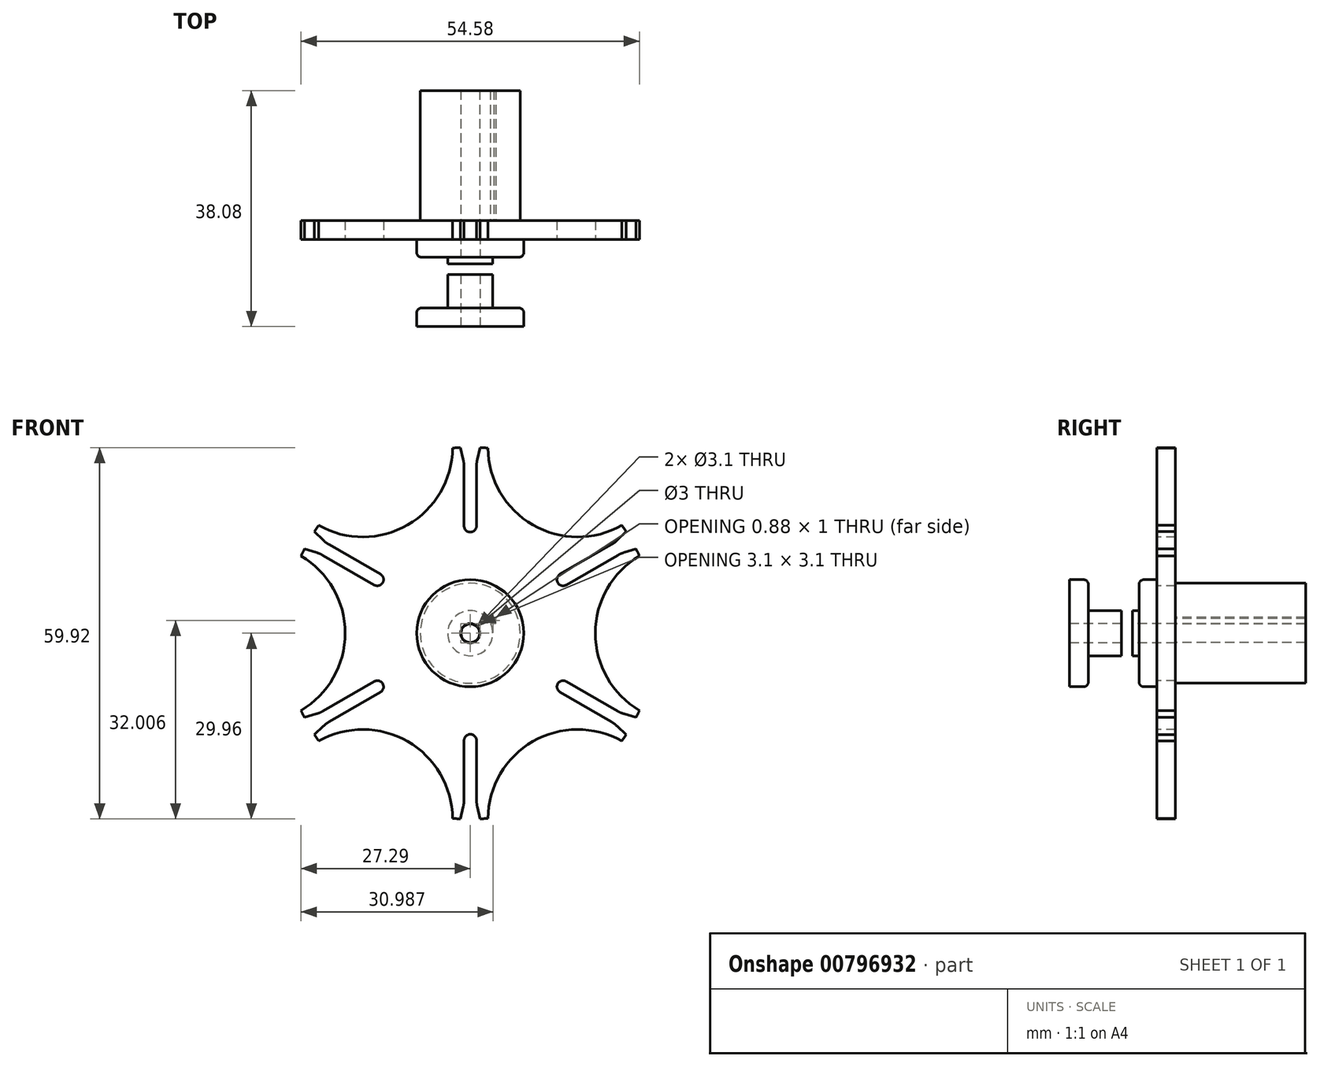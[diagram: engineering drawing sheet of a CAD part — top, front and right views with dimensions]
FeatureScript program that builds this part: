
annotation { "Feature Type Name" : "Feature", "Feature Type Description" : "" }
export const myFeature = defineFeature(function(context is Context, id is Id, definition is map)
    precondition{}
    {
        {
            var Q0;
            Q0=qCreatedBy(makeId("Front.planeOp"),FACE);
            var sketch = newSketch(context, id + "F0", { "sketchPlane" : qUnion([Q0])});
            skCircle(sketch, "E0", {"center": v(0, 0) * mm, "radius": 8.06 * mm});
            skCircle(sketch, "E1", {"center": v(0, 0) * mm, "radius": 3.64 * mm});
            skLineSegment(sketch, "E2", {"start": v(0.57, 3.6) * mm, "end": v(0.57, 4.1) * mm});
            skLineSegment(sketch, "E3", {"start": v(0.57, 4.1) * mm, "end": v(-0.57, 4.1) * mm});
            skLineSegment(sketch, "E4", {"start": v(-0.57, 4.1) * mm, "end": v(-0.57, 3.6) * mm});
            skLineSegment(sketch, "E5", {"start": v(-0.58, 4.1) * mm, "end": v(0, 4.78) * mm});
            skLineSegment(sketch, "E6", {"start": v(0, 4.78) * mm, "end": v(0.57, 4.1) * mm});
            skLineSegment(sketch, "E7.1.0", {"start": v(-3.83, 1.55) * mm, "end": v(-3.4, 1.3) * mm});
            skLineSegment(sketch, "E7.1.1", {"start": v(-2.82, 2.3) * mm, "end": v(-3.26, 2.54) * mm});
            skLineSegment(sketch, "E7.1.2", {"start": v(-3.83, 1.55) * mm, "end": v(-4.14, 2.39) * mm});
            skLineSegment(sketch, "E7.1.3", {"start": v(-4.14, 2.39) * mm, "end": v(-3.26, 2.54) * mm});
            skLineSegment(sketch, "E7.1.4", {"start": v(-3.26, 2.54) * mm, "end": v(-3.83, 1.55) * mm});
            skLineSegment(sketch, "E7.2.0", {"start": v(-3.26, -2.54) * mm, "end": v(-2.82, -2.3) * mm});
            skLineSegment(sketch, "E7.2.1", {"start": v(-3.4, -1.3) * mm, "end": v(-3.83, -1.55) * mm});
            skLineSegment(sketch, "E7.2.2", {"start": v(-3.26, -2.54) * mm, "end": v(-4.14, -2.39) * mm});
            skLineSegment(sketch, "E7.2.3", {"start": v(-4.14, -2.39) * mm, "end": v(-3.83, -1.55) * mm});
            skLineSegment(sketch, "E7.2.4", {"start": v(-3.83, -1.55) * mm, "end": v(-3.26, -2.54) * mm});
            skLineSegment(sketch, "E7.3.0", {"start": v(0.57, -4.1) * mm, "end": v(0.57, -3.6) * mm});
            skLineSegment(sketch, "E7.3.1", {"start": v(-0.58, -3.6) * mm, "end": v(-0.58, -4.1) * mm});
            skLineSegment(sketch, "E7.3.2", {"start": v(0.58, -4.1) * mm, "end": v(0, -4.78) * mm});
            skLineSegment(sketch, "E7.3.3", {"start": v(0, -4.78) * mm, "end": v(-0.58, -4.1) * mm});
            skLineSegment(sketch, "E7.3.4", {"start": v(-0.58, -4.1) * mm, "end": v(0.57, -4.1) * mm});
            skLineSegment(sketch, "E7.4.0", {"start": v(3.83, -1.55) * mm, "end": v(3.4, -1.3) * mm});
            skLineSegment(sketch, "E7.4.1", {"start": v(2.82, -2.3) * mm, "end": v(3.26, -2.54) * mm});
            skLineSegment(sketch, "E7.4.2", {"start": v(3.83, -1.55) * mm, "end": v(4.14, -2.39) * mm});
            skLineSegment(sketch, "E7.4.3", {"start": v(4.14, -2.39) * mm, "end": v(3.26, -2.54) * mm});
            skLineSegment(sketch, "E7.4.4", {"start": v(3.26, -2.54) * mm, "end": v(3.83, -1.55) * mm});
            skLineSegment(sketch, "E7.5.0", {"start": v(3.26, 2.54) * mm, "end": v(2.82, 2.3) * mm});
            skLineSegment(sketch, "E7.5.1", {"start": v(3.4, 1.3) * mm, "end": v(3.83, 1.55) * mm});
            skLineSegment(sketch, "E7.5.2", {"start": v(3.26, 2.54) * mm, "end": v(4.14, 2.39) * mm});
            skLineSegment(sketch, "E7.5.3", {"start": v(4.14, 2.39) * mm, "end": v(3.83, 1.55) * mm});
            skLineSegment(sketch, "E7.5.4", {"start": v(3.83, 1.55) * mm, "end": v(3.26, 2.54) * mm});
            skSolve(sketch);
        }
        {
            var Q0;
            Q0=qCreatedBy(makeId("Front.planeOp"),FACE);
            var sketch = newSketch(context, id + "F1", { "sketchPlane" : qUnion([Q0])});
            skCircle(sketch, "E8", {"center": v(0, 0) * mm, "radius": 30 * mm});
            skLineSegment(sketch, "E9", {"start": v(-1, 29.98) * mm, "end": v(1, 29.98) * mm});
            skLineSegment(sketch, "E10", {"start": v(1, 26.83) * mm, "end": v(1, 17.3) * mm});
            skArc(sketch, "E11", {"start": v(-1, 17.3) * mm, "mid": v(0, 16.3) * mm, "end": v(1, 17.3) * mm});
            skLineSegment(sketch, "E12", {"start": v(-1, 17.3) * mm, "end": v(-1, 26.83) * mm});
            skLineSegment(sketch, "E13", {"start": v(0, 0) * mm, "end": v(0, 9.56) * mm, "construction": true});
            skLineSegment(sketch, "E14", {"start": v(0, 0) * mm, "end": v(17.32, 30) * mm, "construction": true});
            skArc(sketch, "E15", {"start": v(24.44, 17.4) * mm, "mid": v(10.09, 17.47) * mm, "end": v(2.85, 29.86) * mm});
            skLineSegment(sketch, "E16", {"start": v(1.14, 28) * mm, "end": v(1.61, 29.96) * mm});
            skLineSegment(sketch, "E17", {"start": v(-1.14, 28) * mm, "end": v(-1.61, 29.96) * mm});
            skPoint(sketch, "E18.newPointA", {"position": v(-1, 27.43) * mm});
            skArc(sketch, "E18.filletArc", {"start": v(-1, 26.83) * mm, "mid": v(-1.04, 27.43) * mm, "end": v(-1.14, 28) * mm});
            skPoint(sketch, "E19.newPointA", {"position": v(1, 27.43) * mm});
            skPoint(sketch, "E19.newPointB", {"position": v(1, 29.98) * mm});
            skArc(sketch, "E19.filletArc", {"start": v(1.14, 28) * mm, "mid": v(1.04, 27.43) * mm, "end": v(1, 26.83) * mm});
            skArc(sketch, "E20.1.0", {"start": v(-15.49, 7.79) * mm, "mid": v(-14.12, 8.15) * mm, "end": v(-14.49, 9.52) * mm});
            skPoint(sketch, "E20.1.1", {"position": v(-25.47, 15.86) * mm});
            skPoint(sketch, "E20.1.2", {"position": v(-24.26, 12.85) * mm});
            skLineSegment(sketch, "E20.1.3", {"start": v(-22.74, 14.28) * mm, "end": v(-14.49, 9.52) * mm});
            skPoint(sketch, "E20.1.4", {"position": v(-23.26, 14.58) * mm});
            skLineSegment(sketch, "E20.1.5", {"start": v(-15.49, 7.79) * mm, "end": v(-23.74, 12.55) * mm});
            skArc(sketch, "E20.1.6", {"start": v(-2.85, 29.86) * mm, "mid": v(-10.09, 17.47) * mm, "end": v(-24.44, 17.4) * mm});
            skLineSegment(sketch, "E20.1.7", {"start": v(-26.47, 14.13) * mm, "end": v(-25.47, 15.86) * mm});
            skLineSegment(sketch, "E20.1.8", {"start": v(-24.83, 13.02) * mm, "end": v(-26.75, 13.58) * mm});
            skArc(sketch, "E20.1.9", {"start": v(-23.69, 15) * mm, "mid": v(-23.23, 14.6) * mm, "end": v(-22.74, 14.28) * mm});
            skLineSegment(sketch, "E20.1.10", {"start": v(-23.69, 15) * mm, "end": v(-25.14, 16.37) * mm});
            skArc(sketch, "E20.1.11", {"start": v(-23.74, 12.55) * mm, "mid": v(-24.27, 12.82) * mm, "end": v(-24.83, 13.02) * mm});
            skArc(sketch, "E20.2.0", {"start": v(-14.49, -9.52) * mm, "mid": v(-14.12, -8.15) * mm, "end": v(-15.49, -7.79) * mm});
            skPoint(sketch, "E20.2.1", {"position": v(-26.47, -14.13) * mm});
            skPoint(sketch, "E20.2.2", {"position": v(-23.26, -14.58) * mm});
            skLineSegment(sketch, "E20.2.3", {"start": v(-23.74, -12.55) * mm, "end": v(-15.49, -7.79) * mm});
            skPoint(sketch, "E20.2.4", {"position": v(-24.26, -12.85) * mm});
            skLineSegment(sketch, "E20.2.5", {"start": v(-14.49, -9.52) * mm, "end": v(-22.74, -14.28) * mm});
            skArc(sketch, "E20.2.6", {"start": v(-27.29, 12.46) * mm, "mid": v(-20.17, 0) * mm, "end": v(-27.29, -12.46) * mm});
            skLineSegment(sketch, "E20.2.7", {"start": v(-25.47, -15.86) * mm, "end": v(-26.47, -14.13) * mm});
            skLineSegment(sketch, "E20.2.8", {"start": v(-23.69, -15) * mm, "end": v(-25.14, -16.37) * mm});
            skArc(sketch, "E20.2.9", {"start": v(-24.83, -13.02) * mm, "mid": v(-24.27, -12.82) * mm, "end": v(-23.74, -12.55) * mm});
            skLineSegment(sketch, "E20.2.10", {"start": v(-24.83, -13.02) * mm, "end": v(-26.75, -13.58) * mm});
            skArc(sketch, "E20.2.11", {"start": v(-22.74, -14.28) * mm, "mid": v(-23.23, -14.6) * mm, "end": v(-23.69, -15) * mm});
            skArc(sketch, "E20.3.0", {"start": v(1, -17.3) * mm, "mid": v(0, -16.3) * mm, "end": v(-1, -17.3) * mm});
            skPoint(sketch, "E20.3.1", {"position": v(-1, -29.98) * mm});
            skPoint(sketch, "E20.3.2", {"position": v(1, -27.43) * mm});
            skLineSegment(sketch, "E20.3.3", {"start": v(-1, -26.83) * mm, "end": v(-1, -17.3) * mm});
            skPoint(sketch, "E20.3.4", {"position": v(-1, -27.43) * mm});
            skLineSegment(sketch, "E20.3.5", {"start": v(1, -17.3) * mm, "end": v(1, -26.83) * mm});
            skArc(sketch, "E20.3.6", {"start": v(-24.44, -17.4) * mm, "mid": v(-10.09, -17.47) * mm, "end": v(-2.85, -29.86) * mm});
            skLineSegment(sketch, "E20.3.7", {"start": v(1, -29.98) * mm, "end": v(-1, -29.98) * mm});
            skLineSegment(sketch, "E20.3.8", {"start": v(1.14, -28) * mm, "end": v(1.61, -29.96) * mm});
            skArc(sketch, "E20.3.9", {"start": v(-1.14, -28) * mm, "mid": v(-1.04, -27.43) * mm, "end": v(-1, -26.83) * mm});
            skLineSegment(sketch, "E20.3.10", {"start": v(-1.14, -28) * mm, "end": v(-1.61, -29.96) * mm});
            skArc(sketch, "E20.3.11", {"start": v(1, -26.83) * mm, "mid": v(1.04, -27.43) * mm, "end": v(1.14, -28) * mm});
            skArc(sketch, "E20.4.0", {"start": v(15.49, -7.79) * mm, "mid": v(14.12, -8.15) * mm, "end": v(14.49, -9.52) * mm});
            skPoint(sketch, "E20.4.1", {"position": v(25.47, -15.86) * mm});
            skPoint(sketch, "E20.4.2", {"position": v(24.26, -12.85) * mm});
            skLineSegment(sketch, "E20.4.3", {"start": v(22.74, -14.28) * mm, "end": v(14.49, -9.52) * mm});
            skPoint(sketch, "E20.4.4", {"position": v(23.26, -14.58) * mm});
            skLineSegment(sketch, "E20.4.5", {"start": v(15.49, -7.79) * mm, "end": v(23.74, -12.55) * mm});
            skArc(sketch, "E20.4.6", {"start": v(2.85, -29.86) * mm, "mid": v(10.09, -17.47) * mm, "end": v(24.44, -17.4) * mm});
            skLineSegment(sketch, "E20.4.7", {"start": v(26.47, -14.13) * mm, "end": v(25.47, -15.86) * mm});
            skLineSegment(sketch, "E20.4.8", {"start": v(24.83, -13.02) * mm, "end": v(26.75, -13.58) * mm});
            skArc(sketch, "E20.4.9", {"start": v(23.69, -15) * mm, "mid": v(23.23, -14.6) * mm, "end": v(22.74, -14.28) * mm});
            skLineSegment(sketch, "E20.4.10", {"start": v(23.69, -15) * mm, "end": v(25.14, -16.37) * mm});
            skArc(sketch, "E20.4.11", {"start": v(23.74, -12.55) * mm, "mid": v(24.27, -12.82) * mm, "end": v(24.83, -13.02) * mm});
            skArc(sketch, "E20.5.0", {"start": v(14.49, 9.52) * mm, "mid": v(14.12, 8.15) * mm, "end": v(15.49, 7.79) * mm});
            skPoint(sketch, "E20.5.1", {"position": v(26.47, 14.13) * mm});
            skPoint(sketch, "E20.5.2", {"position": v(23.26, 14.58) * mm});
            skLineSegment(sketch, "E20.5.3", {"start": v(23.74, 12.55) * mm, "end": v(15.49, 7.79) * mm});
            skPoint(sketch, "E20.5.4", {"position": v(24.26, 12.85) * mm});
            skLineSegment(sketch, "E20.5.5", {"start": v(14.49, 9.52) * mm, "end": v(22.74, 14.28) * mm});
            skArc(sketch, "E20.5.6", {"start": v(27.29, -12.46) * mm, "mid": v(20.17, 0) * mm, "end": v(27.29, 12.46) * mm});
            skLineSegment(sketch, "E20.5.7", {"start": v(25.47, 15.86) * mm, "end": v(26.47, 14.13) * mm});
            skLineSegment(sketch, "E20.5.8", {"start": v(23.69, 15) * mm, "end": v(25.14, 16.37) * mm});
            skArc(sketch, "E20.5.9", {"start": v(24.83, 13.02) * mm, "mid": v(24.27, 12.82) * mm, "end": v(23.74, 12.55) * mm});
            skLineSegment(sketch, "E20.5.10", {"start": v(24.83, 13.02) * mm, "end": v(26.75, 13.58) * mm});
            skArc(sketch, "E20.5.11", {"start": v(22.74, 14.28) * mm, "mid": v(23.23, 14.6) * mm, "end": v(23.69, 15) * mm});
            skSolve(sketch);
        }
        {
            var Q0;
            Q0=qCreatedBy(makeId("Top.planeOp"),FACE);
            var sketch = newSketch(context, id + "F2", { "sketchPlane" : qUnion([Q0])});
            skLineSegment(sketch, "E21", {"start": v(0, -2.87) * mm, "end": v(0, 0) * mm, "construction": true});
            skLineSegment(sketch, "E22", {"start": v(0, -2.87) * mm, "end": v(3.64, -2.87) * mm, "construction": true});
            skLineSegment(sketch, "E23", {"start": v(3.64, -2.87) * mm, "end": v(7.89, -2.87) * mm});
            skLineSegment(sketch, "E24", {"start": v(8.64, -2.12) * mm, "end": v(8.64, 0.13) * mm});
            skLineSegment(sketch, "E25", {"start": v(8.64, 0.13) * mm, "end": v(0, 0.12) * mm});
            skLineSegment(sketch, "E26", {"start": v(3.64, -2.87) * mm, "end": v(3.64, -3.95) * mm});
            skLineSegment(sketch, "E27", {"start": v(3.64, -11.07) * mm, "end": v(7.89, -11.07) * mm});
            skLineSegment(sketch, "E28", {"start": v(8.64, -11.82) * mm, "end": v(8.64, -14.07) * mm});
            skLineSegment(sketch, "E29", {"start": v(8.64, -14.07) * mm, "end": v(0, -14.08) * mm});
            skLineSegment(sketch, "E30", {"start": v(0, -14.08) * mm, "end": v(0, -5.7) * mm});
            skPoint(sketch, "E31.visualSharp", {"position": v(8.64, -11.07) * mm});
            skArc(sketch, "E31.filletArc", {"start": v(8.64, -11.82) * mm, "mid": v(8.42, -11.3) * mm, "end": v(7.89, -11.07) * mm});
            skPoint(sketch, "E32.visualSharp", {"position": v(8.64, -2.87) * mm});
            skArc(sketch, "E32.filletArc", {"start": v(7.89, -2.88) * mm, "mid": v(8.42, -2.66) * mm, "end": v(8.64, -2.12) * mm});
            skPoint(sketch, "E33.orphan", {"position": v(3.64, 0) * mm});
            skLineSegment(sketch, "E34", {"start": v(3.64, -5.7) * mm, "end": v(0, -5.7) * mm});
            skLineSegment(sketch, "E35", {"start": v(3.64, -3.95) * mm, "end": v(0, -3.95) * mm});
            skLineSegment(sketch, "E36.trimOffspring", {"start": v(3.64, -5.7) * mm, "end": v(3.64, -11.07) * mm});
            skLineSegment(sketch, "E37.trimOffspring", {"start": v(0, -3.95) * mm, "end": v(0, 0.12) * mm});
            skSolve(sketch);
        }
        {
            var Q0;
            Q0=makeQuery(id+"F2.imprint","IMPRINT",FACE,{"disambiguationData":[TD([[makeQuery(id+"F2.imprint","IMPRINT",EDGE,{"derivedFrom":sQuery(id+"F2.wireOp",EDGE,"E23")}),1.0]])]});
            var Q1;
            Q1=makeQuery(id+"F2.imprint","IMPRINT",FACE,{"disambiguationData":[TD([[makeQuery(id+"F2.imprint","IMPRINT",EDGE,{"derivedFrom":sQuery(id+"F2.wireOp",EDGE,"E27")}),-1.0]])]});
            var Q2;
            Q2=sQuery(id+"F2.wireOp",EDGE,"E30");
            revolve(context, id + "F3", {"surfaceOperationType" : NewSurfaceOperationType.NEW, "entities" : qUnion([Q0, Q1]), "axis" : qUnion([Q2]), "revolveType" : RevolveType.FULL});
        }
        {
            var Q0;
            {var subQ13=sQuery(id+"F1.wireOp",EDGE,"E10");Q0=makeQuery(id+"F1.imprint","IMPRINT",FACE,{"disambiguationData":[TD([[makeQuery(id+"F1.imprint","IMPRINT",EDGE,{"derivedFrom":subQ13}),1.0]])]});}
            extrude(context, id + "F4", {"entities" : qUnion([Q0]), "operationType" : NewBodyOperationType.ADD, "depth" : -3 * mm, "offsetDistance" : 25 * mm});
        }
        {
            var Q0;
            Q0=makeQuery(id+"F3.opRevolve","SWEPT_FACE",FACE,{"disambiguationData":[OSD([sQuery(id+"F2.wireOp",EDGE,"E29")])]});
            cPlane(context, id + "F5", {"entities" : qUnion([Q0]), "cplaneType" : CPlaneType.OFFSET, "offset" : 0 * mm, "width" : 150 * mm, "height" : 150 * mm});
        }
        {
            var Q0;
            Q0=qCreatedBy(id+"F5.planeOp",FACE);
            var sketch = newSketch(context, id + "F6", { "sketchPlane" : qUnion([Q0])});
            skPoint(sketch, "E38", {"position": v(0, 0) * mm});
            skSolve(sketch);
        }
        {
            var Q0;
            Q0=sQuery(id+"F6.wireOp",VERTEX,"E38");
            var Q1;
            Q1=makeQuery(id+"F3.opRevolve","SWEPT_BODY",BODY,{"disambiguationData":[OSD([sQuery(id+"F2.wireOp",EDGE,"E27"),sQuery(id+"F2.wireOp",EDGE,"E28"),sQuery(id+"F2.wireOp",EDGE,"E29"),sQuery(id+"F2.wireOp",EDGE,"E30"),sQuery(id+"F2.wireOp",EDGE,"E31.filletArc"),sQuery(id+"F2.wireOp",EDGE,"E34"),sQuery(id+"F2.wireOp",EDGE,"E36.trimOffspring")])]});
            var Q2;
            Q2=makeQuery(id+"F3.opRevolve","SWEPT_BODY",BODY,{"disambiguationData":[OSD([sQuery(id+"F2.wireOp",EDGE,"E23"),sQuery(id+"F2.wireOp",EDGE,"E24"),sQuery(id+"F2.wireOp",EDGE,"E25"),sQuery(id+"F2.wireOp",EDGE,"E26"),sQuery(id+"F2.wireOp",EDGE,"E32.filletArc"),sQuery(id+"F2.wireOp",EDGE,"E35"),sQuery(id+"F2.wireOp",EDGE,"E37.trimOffspring")])]});
            hole(context, id + "F7", {"style" : HoleStyle.SIMPLE, "endStyle" : HoleEndStyle.THROUGH, "holeDiameter" : 3.1 * mm, "majorDiameter" : 5 * mm, "isTappedThrough" : true, "tappedDepth" : 12 * mm, "tapClearance" : 3, "locations" : qUnion([Q0]), "scope" : qUnion([Q1, Q2])});
        }
        {
            var Q0;
            Q0=makeQuery(id+"F0.imprint","IMPRINT",FACE,{"disambiguationData":[TD([[makeQuery(id+"F0.imprint","IMPRINT",EDGE,{"derivedFrom":sQuery(id+"F0.wireOp",EDGE,"E0")}),1.0]])]});
            var Q1;
            {var subQ0=sQuery(id+"F0.wireOp",EDGE,"E7.2.0");Q1=makeQuery(id+"F0.imprint","IMPRINT",FACE,{"disambiguationData":[TD([[makeQuery(id+"F0.imprint","IMPRINT",EDGE,{"derivedFrom":subQ0}),1.0]])]});}
            var Q2;
            Q2=makeQuery(id+"F0.imprint","IMPRINT",FACE,{"disambiguationData":[TD([[makeQuery(id+"F0.imprint","IMPRINT",EDGE,{"derivedFrom":sQuery(id+"F0.wireOp",EDGE,"E7.2.2")}),-1.0]])]});
            var Q3;
            {var subQ0=sQuery(id+"F0.wireOp",EDGE,"E1");var subQ8=makeQuery(id+"F0.imprint","INTERSECT",VERTEX,{"derivedFrom":[subQ0,sQuery(id+"F0.wireOp",EDGE,"E7.5.0")]});Q3=makeQuery(id+"F0.imprint","IMPRINT",FACE,{"disambiguationData":[TD([[makeQuery(id+"F0.imprint","IMPRINT",EDGE,{"disambiguationData":[TD([[subQ8,1.0]])],"derivedFrom":subQ0}),1.0]])]});}
            var Q4;
            {var subQ0=sQuery(id+"F0.wireOp",EDGE,"E7.3.0");Q4=makeQuery(id+"F0.imprint","IMPRINT",FACE,{"disambiguationData":[TD([[makeQuery(id+"F0.imprint","IMPRINT",EDGE,{"derivedFrom":subQ0}),1.0]])]});}
            var Q5;
            {var subQ0=sQuery(id+"F0.wireOp",EDGE,"E7.1.0");Q5=makeQuery(id+"F0.imprint","IMPRINT",FACE,{"disambiguationData":[TD([[makeQuery(id+"F0.imprint","IMPRINT",EDGE,{"derivedFrom":subQ0}),1.0]])]});}
            var Q6;
            {var subQ0=sQuery(id+"F0.wireOp",EDGE,"E2");Q6=makeQuery(id+"F0.imprint","IMPRINT",FACE,{"disambiguationData":[TD([[makeQuery(id+"F0.imprint","IMPRINT",EDGE,{"derivedFrom":subQ0}),1.0]])]});}
            var Q7;
            {var subQ0=sQuery(id+"F0.wireOp",EDGE,"E7.5.0");Q7=makeQuery(id+"F0.imprint","IMPRINT",FACE,{"disambiguationData":[TD([[makeQuery(id+"F0.imprint","IMPRINT",EDGE,{"derivedFrom":subQ0}),1.0]])]});}
            var Q8;
            Q8=makeQuery(id+"F0.imprint","IMPRINT",FACE,{"disambiguationData":[TD([[makeQuery(id+"F0.imprint","IMPRINT",EDGE,{"derivedFrom":sQuery(id+"F0.wireOp",EDGE,"E7.4.2")}),-1.0]])]});
            var Q9;
            Q9=makeQuery(id+"F0.imprint","IMPRINT",FACE,{"disambiguationData":[TD([[makeQuery(id+"F0.imprint","IMPRINT",EDGE,{"derivedFrom":sQuery(id+"F0.wireOp",EDGE,"E7.3.2")}),-1.0]])]});
            var Q10;
            Q10=makeQuery(id+"F0.imprint","IMPRINT",FACE,{"disambiguationData":[TD([[makeQuery(id+"F0.imprint","IMPRINT",EDGE,{"derivedFrom":sQuery(id+"F0.wireOp",EDGE,"E7.1.2")}),-1.0]])]});
            var Q11;
            Q11=makeQuery(id+"F0.imprint","IMPRINT",FACE,{"disambiguationData":[TD([[makeQuery(id+"F0.imprint","IMPRINT",EDGE,{"derivedFrom":sQuery(id+"F0.wireOp",EDGE,"E3")}),-1.0]])]});
            var Q12;
            {var subQ0=sQuery(id+"F0.wireOp",EDGE,"E7.4.0");Q12=makeQuery(id+"F0.imprint","IMPRINT",FACE,{"disambiguationData":[TD([[makeQuery(id+"F0.imprint","IMPRINT",EDGE,{"derivedFrom":subQ0}),1.0]])]});}
            extrude(context, id + "F8", {"entities" : qUnion([Q0, Q1, Q2, Q3, Q4, Q5, Q6, Q7, Q8, Q9, Q10, Q11, Q12]), "oppositeDirection" : true, "depth" : 24 * mm, "offsetDistance" : 25 * mm, "hasSecondDirection" : true, "secondDirectionOppositeDirection" : true, "secondDirectionDepth" : 3 * mm});
        }
        {
            var Q0;
            Q0=sQuery(id+"F0.wireOp",VERTEX,"E0.center");
            var Q1;
            Q1=makeQuery(id+"F8.opExtrude","SWEPT_BODY",BODY,{"disambiguationData":[OSD([sQuery(id+"F0.wireOp",EDGE,"E0")])]});
            hole(context, id + "F9", {"style" : HoleStyle.SIMPLE, "endStyle" : HoleEndStyle.THROUGH, "holeDiameter" : 3 * mm, "majorDiameter" : 5 * mm, "isTappedThrough" : true, "tappedDepth" : 12 * mm, "tapClearance" : 3, "locations" : qUnion([Q0]), "scope" : qUnion([Q1])});
        }
    });
